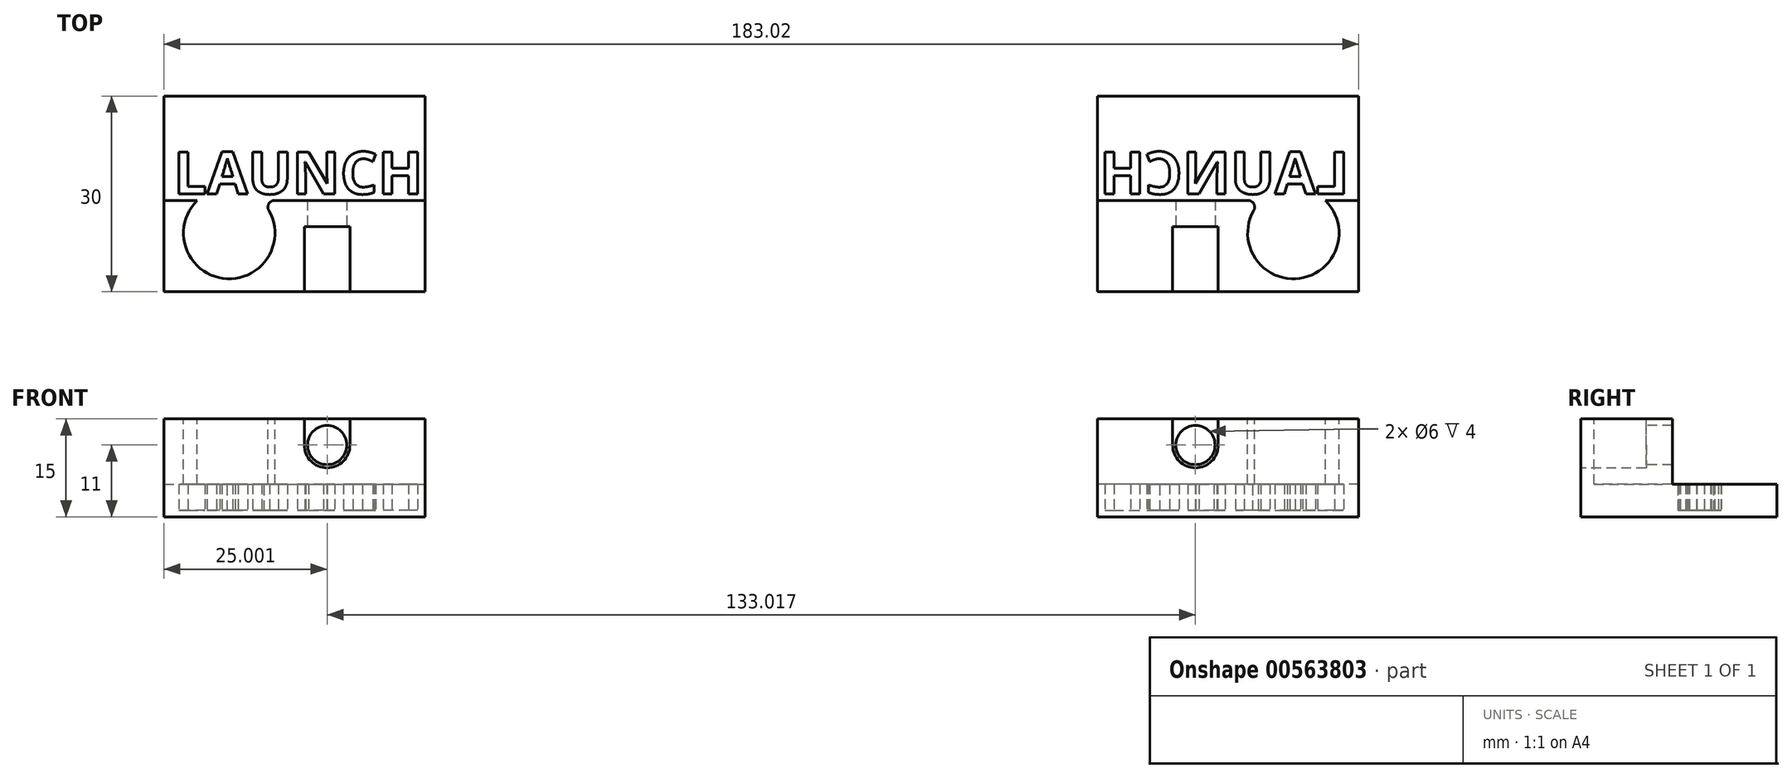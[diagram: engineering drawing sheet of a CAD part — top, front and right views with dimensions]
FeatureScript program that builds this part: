
annotation { "Feature Type Name" : "Feature", "Feature Type Description" : "" }
export const myFeature = defineFeature(function(context is Context, id is Id, definition is map)
    precondition{}
    {
        {
            var Q0;
            Q0=qCreatedBy(makeId("Top.planeOp"),FACE);
            var sketch = newSketch(context, id + "F0", { "sketchPlane" : qUnion([Q0])});
            skLineSegment(sketch, "E0.bottom", {"start": v(-91.5, 40.33) * mm, "end": v(-51.5, 40.33) * mm});
            skLineSegment(sketch, "E0.top", {"start": v(-91.5, 10.33) * mm, "end": v(-51.5, 10.33) * mm});
            skLineSegment(sketch, "E0.left", {"start": v(-91.5, 40.33) * mm, "end": v(-91.5, 10.33) * mm});
            skLineSegment(sketch, "E0.right", {"start": v(-51.5, 40.33) * mm, "end": v(-51.5, 10.33) * mm});
            skSolve(sketch);
        }
        {
            var Q0;
            Q0=qSketchRegion(id+"F0",true);
            extrude(context, id + "F1", {"entities" : qUnion([Q0]), "depth" : 1 * mm, "offsetDistance" : 25 * mm});
        }
        {
            var Q0;
            Q0=makeQuery(id+"F1.opExtrude","CAP_FACE",FACE,{"disambiguationData":[OSD([sQuery(id+"F0.wireOp",EDGE,"E0.bottom"),sQuery(id+"F0.wireOp",EDGE,"E0.top"),sQuery(id+"F0.wireOp",EDGE,"E0.left"),sQuery(id+"F0.wireOp",EDGE,"E0.right")])],"isStart":false});
            var sketch = newSketch(context, id + "F2", { "sketchPlane" : qUnion([Q0])});
            skLineSegment(sketch, "E1.bottom", {"start": v(-90, 31.83) * mm, "end": v(-52.09, 31.83) * mm});
            skLineSegment(sketch, "E1.top", {"start": v(-90, 25.33) * mm, "end": v(-52.09, 25.33) * mm});
            skLineSegment(sketch, "E1.left", {"start": v(-90, 31.83) * mm, "end": v(-90, 25.33) * mm});
            skLineSegment(sketch, "E1.right", {"start": v(-52.09, 31.83) * mm, "end": v(-52.09, 25.33) * mm});
            skLineSegment(sketch, "E2", {"start": v(-51.5, 24.33) * mm, "end": v(-91.5, 24.33) * mm});
            skText(sketch, "E3", { "text": "LAUNCH", "fontName": "OpenSans-Bold.ttf"});
            const initialGuessF2  = {"E3": [-0.09, 0.02533, 1, 0, 0.0065]};
            skSetInitialGuess(sketch, initialGuessF2);
            skSolve(sketch);
        }
        {
            var Q0;
            {var subQ1=sQuery(id+"F2.wireOp",EDGE,"E1.left");Q0=makeQuery(id+"F2.imprint","IMPRINT",FACE,{"disambiguationData":[TD([[makeQuery(id+"F2.imprint","IMPRINT",EDGE,{"derivedFrom":subQ1}),1.0]])]});}
            var Q1;
            {var subQ12=sQuery(id+"F2.wireOp",EDGE,"E1.right");Q1=makeQuery(id+"F2.imprint","IMPRINT",FACE,{"disambiguationData":[TD([[makeQuery(id+"F2.imprint","IMPRINT",EDGE,{"derivedFrom":subQ12}),-1.0]])]});}
            var Q2;
            Q2=makeQuery(id+"F2.imprint","IMPRINT",FACE,{"disambiguationData":[TD([[makeQuery(id+"F2.imprint","IMPRINT",EDGE,{"derivedFrom":sQuery(id+"F2.wireOp",EDGE,"51396a01-1bfa-4c7b-8087-b3bf958994e2.sketch_text.stroke-44")}),1.0]])]});
            var Q3;
            {var subQ0=sQuery(id+"F2.wireOp",EDGE,"51396a01-1bfa-4c7b-8087-b3bf958994e2.sketch_text.stroke-36");Q3=makeQuery(id+"F2.imprint","IMPRINT",FACE,{"disambiguationData":[TD([[makeQuery(id+"F2.imprint","IMPRINT",EDGE,{"derivedFrom":subQ0}),1.0]])]});}
            var Q4;
            Q4=makeQuery(id+"F2.imprint","IMPRINT",FACE,{"disambiguationData":[TD([[makeQuery(id+"F2.imprint","IMPRINT",EDGE,{"derivedFrom":sQuery(id+"F2.wireOp",EDGE,"51396a01-1bfa-4c7b-8087-b3bf958994e2.sketch_text.stroke-48")}),1.0]])]});
            var Q5;
            {var subQ0=sQuery(id+"F2.wireOp",EDGE,"51396a01-1bfa-4c7b-8087-b3bf958994e2.sketch_text.stroke-55");Q5=makeQuery(id+"F2.imprint","IMPRINT",FACE,{"disambiguationData":[TD([[makeQuery(id+"F2.imprint","IMPRINT",EDGE,{"derivedFrom":subQ0}),1.0]])]});}
            extrude(context, id + "F3", {"entities" : qUnion([Q0, Q1, Q2, Q3, Q4, Q5]), "operationType" : NewBodyOperationType.ADD, "depth" : 4 * mm, "offsetDistance" : 25 * mm});
        }
        {
            var Q0;
            {var subQ10=sQuery(id+"F2.wireOp",EDGE,"E1.left");Q0=makeQuery(id+"F2.imprint","IMPRINT",FACE,{"disambiguationData":[TD([[makeQuery(id+"F2.imprint","IMPRINT",EDGE,{"derivedFrom":subQ10}),-1.0]])]});}
            var Q1;
            {var subQ13=makeQuery(id+"F1.opExtrude","CAP_EDGE",EDGE,{"disambiguationData":[OSD([sQuery(id+"F0.wireOp",EDGE,"E0.top")])],"isStart":false});Q1=makeQuery(id+"F2.imprint","IMPRINT",FACE,{"disambiguationData":[TD([[makeQuery(id+"F2.imprint","IMPRINT",EDGE,{"derivedFrom":subQ13}),1.0]])]});}
            var Q2;
            {var subQ0=sQuery(id+"F2.wireOp",EDGE,"E3.sketch_text.stroke-63");Q2=makeQuery(id+"F2.imprint","IMPRINT",FACE,{"disambiguationData":[TD([[makeQuery(id+"F2.imprint","IMPRINT",EDGE,{"derivedFrom":subQ0}),1.0]])]});}
            var Q3;
            Q3=makeQuery(id+"F2.imprint","IMPRINT",FACE,{"disambiguationData":[TD([[makeQuery(id+"F2.imprint","IMPRINT",EDGE,{"derivedFrom":sQuery(id+"F2.wireOp",EDGE,"E3.sketch_text.stroke-14")}),1.0]])]});
            var Q4;
            {var subQ0=sQuery(id+"F2.wireOp",EDGE,"E3.sketch_text.stroke-6");Q4=makeQuery(id+"F2.imprint","IMPRINT",FACE,{"disambiguationData":[TD([[makeQuery(id+"F2.imprint","IMPRINT",EDGE,{"derivedFrom":subQ0}),1.0]])]});}
            var Q5;
            {var subQ0=sQuery(id+"F2.wireOp",EDGE,"E3.sketch_text.stroke-34");Q5=makeQuery(id+"F2.imprint","IMPRINT",FACE,{"disambiguationData":[TD([[makeQuery(id+"F2.imprint","IMPRINT",EDGE,{"derivedFrom":subQ0}),1.0]])]});}
            extrude(context, id + "F4", {"entities" : qUnion([Q0, Q1, Q2, Q3, Q4, Q5]), "operationType" : NewBodyOperationType.ADD, "depth" : 4 * mm, "offsetDistance" : 25 * mm});
        }
        {
            var Q0;
            {var subQ13=makeQuery(id+"F1.opExtrude","CAP_EDGE",EDGE,{"disambiguationData":[OSD([sQuery(id+"F0.wireOp",EDGE,"E0.top")])],"isStart":false});Q0=makeQuery(id+"F2.imprint","IMPRINT",FACE,{"disambiguationData":[TD([[makeQuery(id+"F2.imprint","IMPRINT",EDGE,{"derivedFrom":subQ13}),1.0]])]});}
            extrude(context, id + "F5", {"entities" : qUnion([Q0]), "operationType" : NewBodyOperationType.ADD, "depth" : 14 * mm, "offsetDistance" : 25 * mm});
        }
        {
            var Q0;
            {var subQ0=sQuery(id+"F0.wireOp",EDGE,"E0.top");Q0=makeQuery(id+"F5.boolean.opBoolean","MERGE",FACE,{"derivedFrom":[makeQuery(id+"F4.boolean.opBoolean","MERGE",FACE,{"derivedFrom":[makeQuery(id+"F1.opExtrude","SWEPT_FACE",FACE,{"disambiguationData":[OSD([subQ0])]}),makeQuery(id+"F4.opExtrude","SWEPT_FACE",FACE,{"disambiguationData":[OSD([subQ0])]})]}),makeQuery(id+"F5.opExtrude","SWEPT_FACE",FACE,{"disambiguationData":[OSD([subQ0])]})]});}
            var sketch = newSketch(context, id + "F6", { "sketchPlane" : qUnion([Q0])});
            skCircle(sketch, "E4", {"center": v(-66.5, 11) * mm, "radius": 3 * mm});
            skArc(sketch, "E5", {"start": v(-70, 11) * mm, "mid": v(-66.5, 7.5) * mm, "end": v(-63, 11) * mm});
            skLineSegment(sketch, "E6", {"start": v(-63, 11) * mm, "end": v(-63, 15) * mm});
            skLineSegment(sketch, "E7", {"start": v(-70, 11) * mm, "end": v(-70, 15) * mm});
            skSolve(sketch);
        }
        {
            var Q0;
            Q0=makeQuery(id+"F6.imprint","IMPRINT",FACE,{"disambiguationData":[TD([[makeQuery(id+"F6.imprint","IMPRINT",EDGE,{"derivedFrom":sQuery(id+"F6.wireOp",EDGE,"E4")}),1.0]])]});
            extrude(context, id + "F7", {"entities" : qUnion([Q0]), "operationType" : NewBodyOperationType.REMOVE, "oppositeDirection" : true, "depth" : 14 * mm, "offsetDistance" : 25 * mm});
        }
        {
            var Q0;
            Q0=makeQuery(id+"F5.opExtrude","CAP_FACE",FACE,{"disambiguationData":[OSD([sQuery(id+"F0.wireOp",EDGE,"E0.top"),sQuery(id+"F0.wireOp",EDGE,"E0.left"),sQuery(id+"F0.wireOp",EDGE,"E0.right"),sQuery(id+"F2.wireOp",EDGE,"E2")])],"isStart":false});
            var sketch = newSketch(context, id + "F8", { "sketchPlane" : qUnion([Q0])});
            skCircle(sketch, "E8", {"center": v(-81.5, 19.33) * mm, "radius": 7 * mm});
            skSolve(sketch);
        }
        {
            var Q0;
            {var subQ0=sQuery(id+"F8.wireOp",EDGE,"E8");var subQ1=makeQuery(id+"F5.opExtrude","CAP_EDGE",EDGE,{"disambiguationData":[OSD([sQuery(id+"F2.wireOp",EDGE,"E2")])],"isStart":false});var subQ2=makeQuery(id+"F8.imprint","INTERSECT",VERTEX,{"disambiguationData":[OD(0.0)],"derivedFrom":[subQ1,subQ0]});Q0=makeQuery(id+"F8.imprint","IMPRINT",FACE,{"disambiguationData":[TD([[makeQuery(id+"F8.imprint","IMPRINT",EDGE,{"disambiguationData":[TD([[subQ2,1.0]])],"derivedFrom":subQ0}),1.0]])]});}
            extrude(context, id + "F9", {"entities" : qUnion([Q0]), "operationType" : NewBodyOperationType.REMOVE, "oppositeDirection" : true, "depth" : 10 * mm, "offsetDistance" : 25 * mm});
        }
        {
            var Q0;
            {var subQ0=sQuery(id+"F8.wireOp",EDGE,"E8");var subQ1=sQuery(id+"F2.wireOp",EDGE,"E2");Q0=makeQuery(id+"F9.boolean.opBoolean","COPY",EDGE,{"derivedFrom":makeQuery(id+"F9.opExtrude","SWEPT_EDGE",EDGE,{"disambiguationData":[OSD([subQ1,subQ0]),TDD([makeQuery(id+"F8.imprint","INTERSECT",VERTEX,{"disambiguationData":[OD(0.0)],"derivedFrom":[makeQuery(id+"F5.opExtrude","CAP_EDGE",EDGE,{"disambiguationData":[OSD([subQ1])],"isStart":false}),subQ0]})])]})});}
            var Q1;
            {var subQ0=sQuery(id+"F8.wireOp",EDGE,"E8");var subQ1=sQuery(id+"F2.wireOp",EDGE,"E2");Q1=makeQuery(id+"F9.boolean.opBoolean","COPY",EDGE,{"derivedFrom":makeQuery(id+"F9.opExtrude","SWEPT_EDGE",EDGE,{"disambiguationData":[OSD([subQ1,subQ0]),TDD([makeQuery(id+"F8.imprint","INTERSECT",VERTEX,{"disambiguationData":[OD(1.0)],"derivedFrom":[makeQuery(id+"F5.opExtrude","CAP_EDGE",EDGE,{"disambiguationData":[OSD([subQ1])],"isStart":false}),subQ0]})])]})});}
            fillet(context, id + "F10", {"entities" : qUnion([Q0, Q1]), "radius" : 1 * mm, "tangentPropagation" : true, "allowEdgeOverflow" : false});
        }
        {
            var Q0;
            Q0=makeQuery(id+"F6.imprint","IMPRINT",FACE,{"disambiguationData":[TD([[makeQuery(id+"F6.imprint","IMPRINT",EDGE,{"derivedFrom":sQuery(id+"F6.wireOp",EDGE,"E4")}),-1.0]])]});
            var Q1;
            Q1=sQuery(id+"F6.wireOp",EDGE,"E5");
            extrude(context, id + "F11", {"entities" : qUnion([Q0]), "operationType" : NewBodyOperationType.REMOVE, "surfaceEntities" : qUnion([Q1]), "oppositeDirection" : true, "depth" : 10 * mm, "offsetDistance" : 25 * mm});
        }
        {
            var Q0;
            Q0=makeQuery(id+"F1.opExtrude","SWEPT_BODY",BODY,{"disambiguationData":[OSD([sQuery(id+"F0.wireOp",EDGE,"E0.bottom"),sQuery(id+"F0.wireOp",EDGE,"E0.top"),sQuery(id+"F0.wireOp",EDGE,"E0.left"),sQuery(id+"F0.wireOp",EDGE,"E0.right")])]});
            var Q1;
            Q1=qCreatedBy(makeId("Right.planeOp"),FACE);
            mirror(context, id + "F12", {"entities" : qUnion([Q0]), "mirrorPlane" : qUnion([Q1])});
        }
    });
